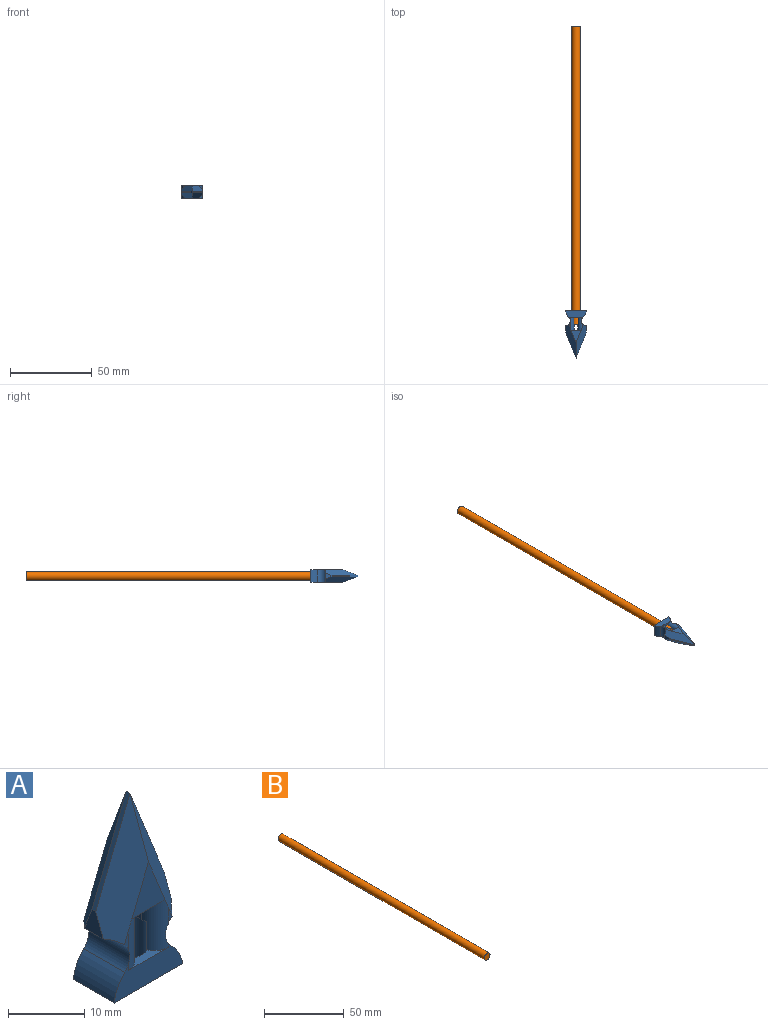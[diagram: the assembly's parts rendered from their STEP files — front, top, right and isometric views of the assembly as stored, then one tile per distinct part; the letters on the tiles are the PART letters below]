
ASSEMBLY  parts=2 mates=1
PART A: 33 faces, bbox 12.7x7.6x28.9 mm
  f0: plane 7.62x6.1mm, normal (0,1,0), area 23.2mm2, adj f18,f19,f24
  f1: plane 3.31x0.8mm, normal (0,1,0), area 1.2mm2, adj f16,f18,f30
  f2: plane 12.7x5.23mm, normal (0,1,0), area 44.7mm2, adj f12,f16,f17,f22,f23,f25,f30,f32
  f3: plane 3.31x0.8mm, normal (0,-1,0), area 1.2mm2, adj f16,f21,f29
  f4: plane 7.62x6.1mm, normal (0,-1,0), area 23.2mm2, adj f20,f21,f24
  f5: plane 2.49x0.69mm, normal (0,-1,0), area 0.8mm2, adj f17,f20,f31
  f6: plane 12.7x5.23mm, normal (0,-1,0), area 44.7mm2, adj f12,f16,f17,f22,f23,f26,f29,f31
  f7: plane 2.49x0.69mm, normal (0,1,0), area 0.8mm2, adj f17,f19,f32
  f8: cylinder r=2.54mm len=8.47mm, axis (0,0,1), area 110.4mm2, adj f9,f10,f12,f25,f26,f29,f30,f31
  f9: plane 4.38x1.43mm, normal (0,0,-1), area 4.6mm2, adj f8,f27,f29,f30
  f10: plane 4.34x1.39mm, normal (0,0,-1), area 4.4mm2, adj f8,f28,f31,f32
  f11: plane 3.69x3.45mm, normal (1,0,0), area 7.7mm2, adj f13,f17,f19,f20
  f12: plane 12.7x7.62mm, normal (0,0,-1), area 76.5mm2, adj f2,f6,f8,f22,f23
  f13: plane 15.88x6.35mm, normal (0.93,0,0.37), area 12.2mm2, adj f11,f14,f19,f20
  f14: plane 15.88x6.35mm, normal (-0.93,0,0.37), area 12.2mm2, adj f13,f15,f18,f21
  f15: plane 3.7x3.46mm, normal (-1,0,0), area 7.7mm2, adj f14,f16,f18,f21
  f16: cylinder r=3.11mm len=7.62mm, axis (0,-1,0), area 49.3mm2, adj f1,f2,f3,f6,f15,f18,f21,f23
  f17: cylinder r=3.11mm len=7.62mm, axis (0,-1,0), area 52.4mm2, adj f2,f5,f6,f7,f11,f19,f20,f22
  f18: plane 20.47x6.38mm, normal (-0.66,0.71,0.26), area 75.6mm2, adj f0,f1,f14,f15,f16,f19,f24,f30
  f19: plane 20.28x6.38mm, normal (0.66,0.71,0.26), area 75.3mm2, adj f0,f7,f11,f13,f17,f18,f24,f32
  f20: plane 20.28x6.38mm, normal (0.66,-0.71,0.26), area 75.3mm2, adj f4,f5,f11,f13,f17,f21,f24,f31
  f21: plane 20.47x6.38mm, normal (-0.66,-0.71,0.26), area 75.6mm2, adj f3,f4,f14,f15,f16,f20,f24,f29
  f22: cylinder r=6.92mm len=7.62mm, axis (0,1,0), area 34.3mm2, adj f2,f6,f12,f17
  f23: cylinder r=6.92mm len=7.62mm, axis (0,-1,0), area 34.3mm2, adj f2,f6,f12,f16
  f24: plane 7.62x6.23mm, normal (0,0,-1), area 22.7mm2, adj f0,f4,f18,f19,f20,f21,f27,f28
  f25: plane 7.34x1.64mm, normal (0,0,1), area 5.7mm2, adj f2,f8,f30,f32
  f26: plane 7.34x1.64mm, normal (0,0,1), area 5.7mm2, adj f6,f8,f29,f31
  f27: plane 3.45x2.54mm, normal (1,0,0), area 8.8mm2, adj f9,f24,f29,f30
  f28: plane 3.45x2.54mm, normal (-1,0,0), area 8.8mm2, adj f10,f24,f31,f32
  f29: cylinder r=2.54mm len=7.98mm, axis (0,0,1), area 27mm2, adj f3,f6,f8,f9,f16,f21,f24,f26
  f30: cylinder r=2.54mm len=7.98mm, axis (0,0,-1), area 27mm2, adj f1,f2,f8,f9,f16,f18,f24,f25
  f31: cylinder r=2.54mm len=7.98mm, axis (0,0,-1), area 26.1mm2, adj f5,f6,f8,f10,f17,f20,f24,f26
  f32: cylinder r=2.54mm len=7.98mm, axis (0,0,1), area 26.1mm2, adj f2,f7,f8,f10,f17,f19,f24,f25
PART B: 3 faces, bbox 5.1x182.4x5.1 mm
  f0: cylinder r=2.54mm len=182.37mm, axis (0,1,0), area 2910.5mm2, adj f1,f2
  f1: plane 5.08x5.08mm, normal (0,-1,0), area 20.3mm2, adj f0
  f2: plane 5.08x5.08mm, normal (0,1,0), area 20.3mm2, adj f0
PLACE A rot(axis=(1,0,0),90deg) t=(0,-74.42,0)mm
PLACE B at identity
MATE fastened A.f8 <-> B.f0  axis (0,1,0) through (0,-74.42,0)mm
